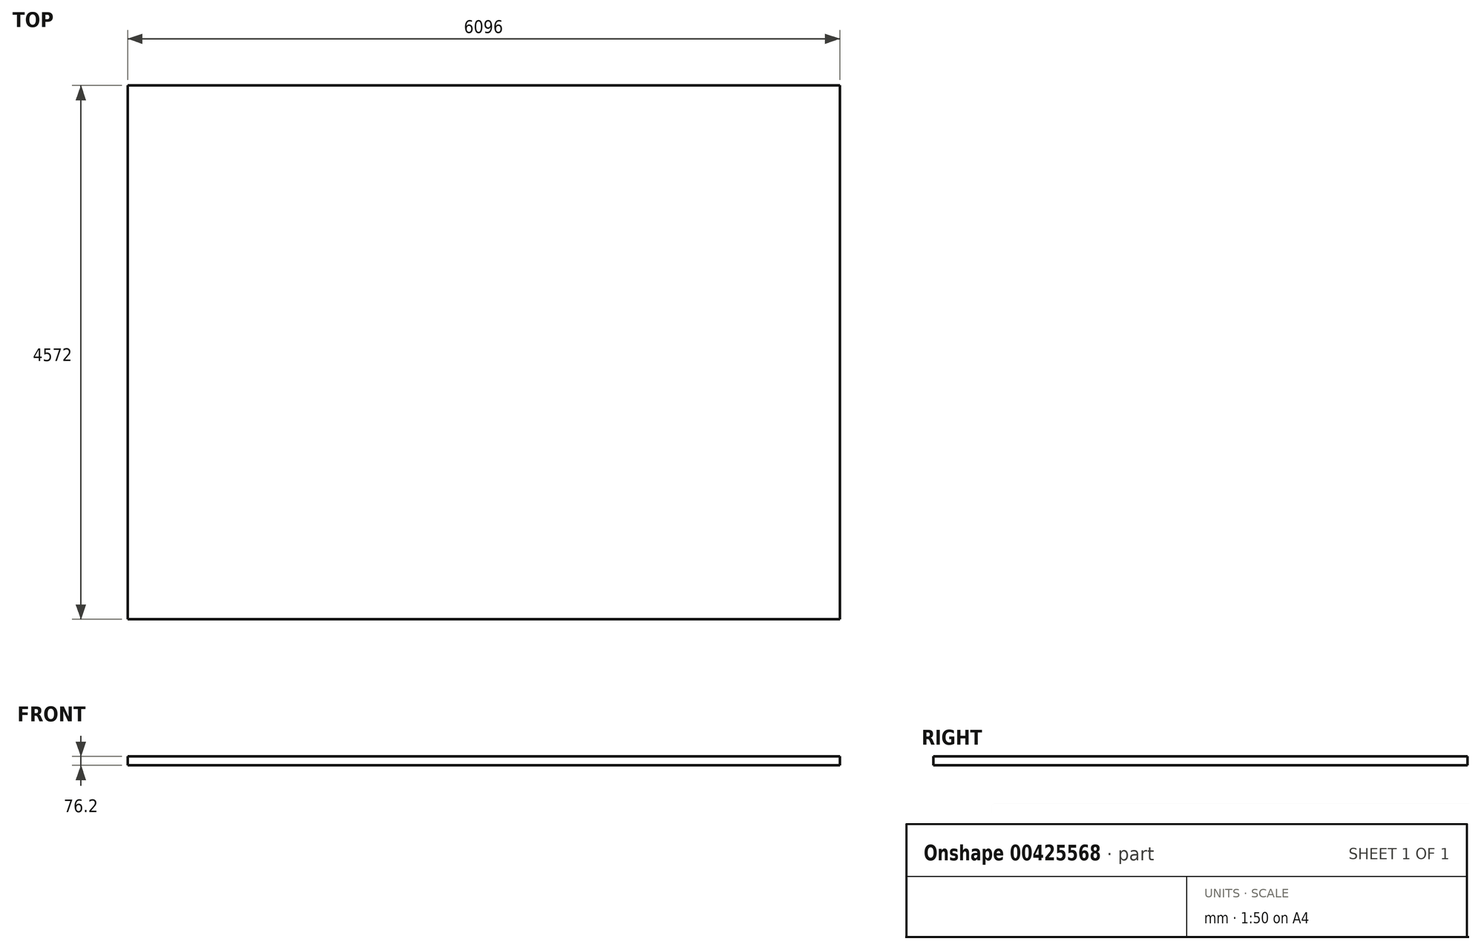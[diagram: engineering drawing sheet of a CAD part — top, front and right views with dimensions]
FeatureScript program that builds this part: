
annotation { "Feature Type Name" : "Feature", "Feature Type Description" : "" }
export const myFeature = defineFeature(function(context is Context, id is Id, definition is map)
    precondition{}
    {
        {
            var Q0;
            Q0=qCreatedBy(makeId("Top.planeOp"),FACE);
            var sketch = newSketch(context, id + "F0", { "sketchPlane" : qUnion([Q0])});
            skLineSegment(sketch, "E0.bottom", {"start": v(3048, 2286) * mm, "end": v(-3048, 2286) * mm});
            skLineSegment(sketch, "E0.top", {"start": v(3048, -2286) * mm, "end": v(-3048, -2286) * mm});
            skLineSegment(sketch, "E0.left", {"start": v(3048, 2286) * mm, "end": v(3048, -2286) * mm});
            skLineSegment(sketch, "E0.right", {"start": v(-3048, 2286) * mm, "end": v(-3048, -2286) * mm});
            skPoint(sketch, "E0.middle", {"position": v(0, 0) * mm});
            skSolve(sketch);
        }
        {
            var Q0;
            Q0 = qSketchRegion(id + "F0", true);
            extrude(context, id + "F1", {"entities" : qUnion([Q0]), "oppositeDirection" : true, "depth" : 76.2 * mm});
        }
    });
